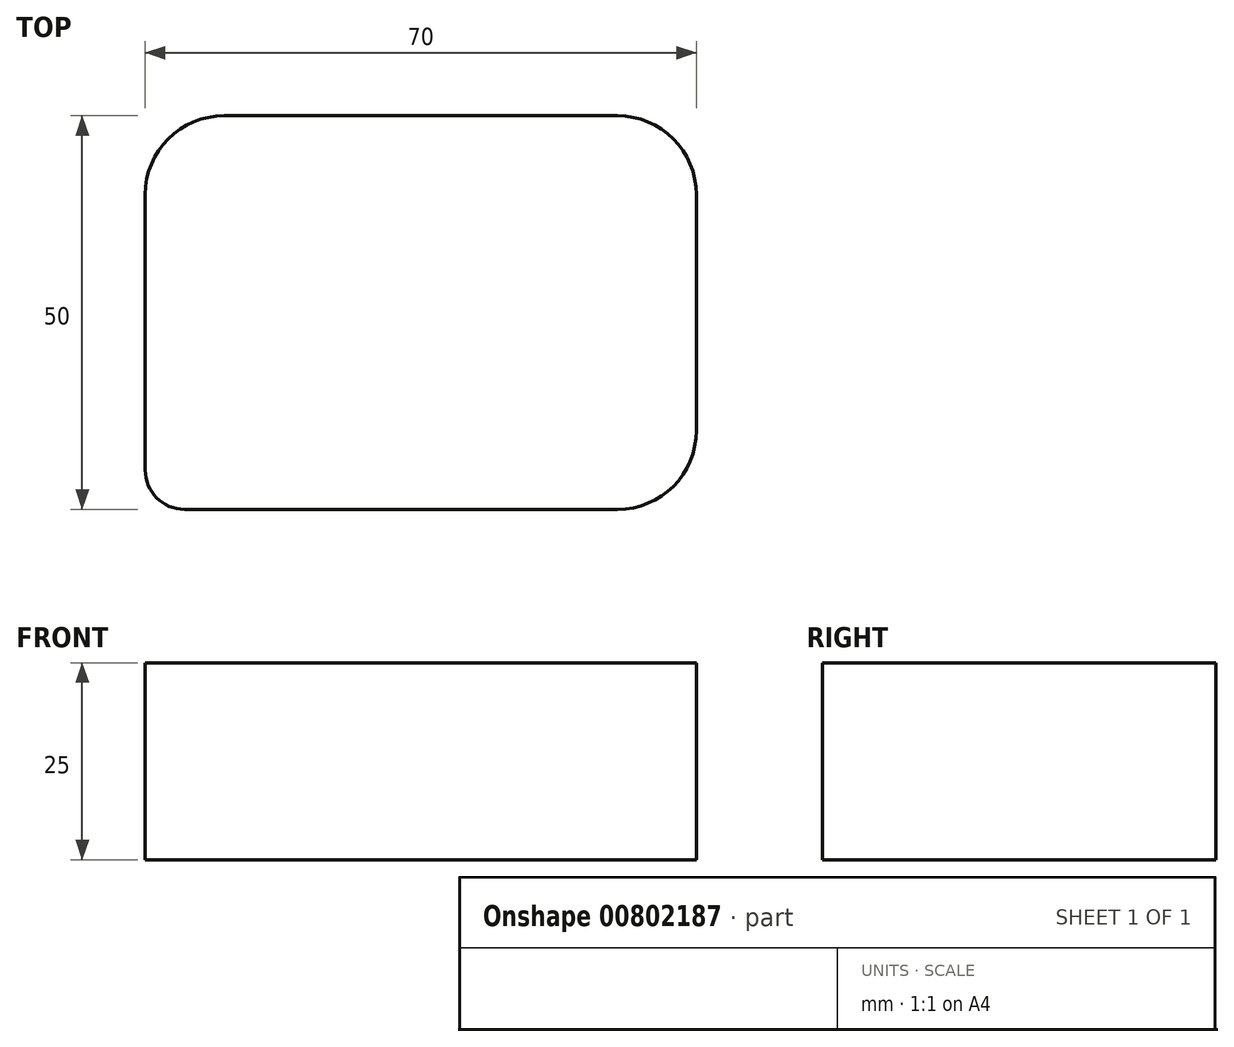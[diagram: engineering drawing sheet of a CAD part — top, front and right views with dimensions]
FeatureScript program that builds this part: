
annotation { "Feature Type Name" : "Feature", "Feature Type Description" : "" }
export const myFeature = defineFeature(function(context is Context, id is Id, definition is map)
    precondition{}
    {
        {
            var Q0;
            Q0=qCreatedBy(makeId("Top.planeOp"),FACE);
            var sketch = newSketch(context, id + "F0", { "sketchPlane" : qUnion([Q0])});
            skLineSegment(sketch, "E0.bottom", {"start": v(10, 0) * mm, "end": v(60, 0) * mm});
            skLineSegment(sketch, "E0.top", {"start": v(5, -50) * mm, "end": v(60, -50) * mm});
            skLineSegment(sketch, "E0.left", {"start": v(0, -10) * mm, "end": v(0, -45) * mm});
            skLineSegment(sketch, "E0.right", {"start": v(70, -10) * mm, "end": v(70, -40) * mm});
            skPoint(sketch, "E1.visualSharp", {"position": v(0, -50) * mm});
            skArc(sketch, "E1.filletArc", {"start": v(0, -45) * mm, "mid": v(1.46, -48.54) * mm, "end": v(5, -50) * mm});
            skPoint(sketch, "E2.visualSharp", {"position": v(0, 0) * mm});
            skArc(sketch, "E2.filletArc", {"start": v(10, 0) * mm, "mid": v(2.93, -2.93) * mm, "end": v(0, -10) * mm});
            skPoint(sketch, "E3.visualSharp", {"position": v(70, 0) * mm});
            skArc(sketch, "E3.filletArc", {"start": v(70, -10) * mm, "mid": v(67.07, -2.93) * mm, "end": v(60, 0) * mm});
            skPoint(sketch, "E4.visualSharp", {"position": v(70, -50) * mm});
            skArc(sketch, "E4.filletArc", {"start": v(60, -50) * mm, "mid": v(67.07, -47.07) * mm, "end": v(70, -40) * mm});
            skSolve(sketch);
        }
        {
            var Q0;
            Q0 = qSketchRegion(id + "F0", true);
            extrude(context, id + "F1", {"entities" : qUnion([Q0]), "depth" : 25 * mm, "offsetDistance" : 25 * mm});
        }
    });
